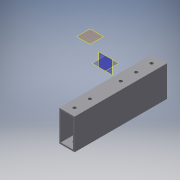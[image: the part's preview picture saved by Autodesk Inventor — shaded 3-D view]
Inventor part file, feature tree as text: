
AUTODESK INVENTOR PART (.ipt)
format: ipt  version: 2018 (Build 220112000, 112)  size: 144,384 bytes
history: native  units: in
note: dims shown in document units (in); Inventor stores cm internally (conversion verified against a paired STEP export)
features: plane x4, extrude x3, sketch x3
ambient origin geometry x8: Origin, YZ Plane, XZ Plane, XY Plane, X Axis, Y Axis, Z Axis, Center Point
bodies: Body1 (feature_tree)
feature tree (10):
  plane  "Work Plane1"
  extrude  "Extrusion13"  Depth=1.0in
  plane  "Work Plane4"
  plane  "Work Plane3"
  extrude  "Extrusion16"  Depth=0.1in
  plane  "Work Plane2"
  extrude  "Extrusion20"  Depth=0.1in
  sketch  "Sketch16"  dims[d48=0.1in d54=1.0in]
  sketch  "Sketch20"  dims[d55=2.0in d56=0.1in]
  sketch  "Sketch24"  dims[d57=0.1in d58=0.1in d59=0.1in d60=6.0in d61=0.0in d71=0.5in d72=0.5in d73=0.5in d74=0.2031in d75=0.2031in d76=0.2031in d77=0.5in d78=0.5in d79=0.2031in d80=0.2031in d81=0.5in d82=1.0in d83=1.0in d84=1.0in d85=1.0in d86=3.0in d87=0.0in d112=0.5in d113=1.0in d114=0.2031in d115=0.2031in d116=0.5in d117=0.5in d118=2.0in d119=0.0in]
